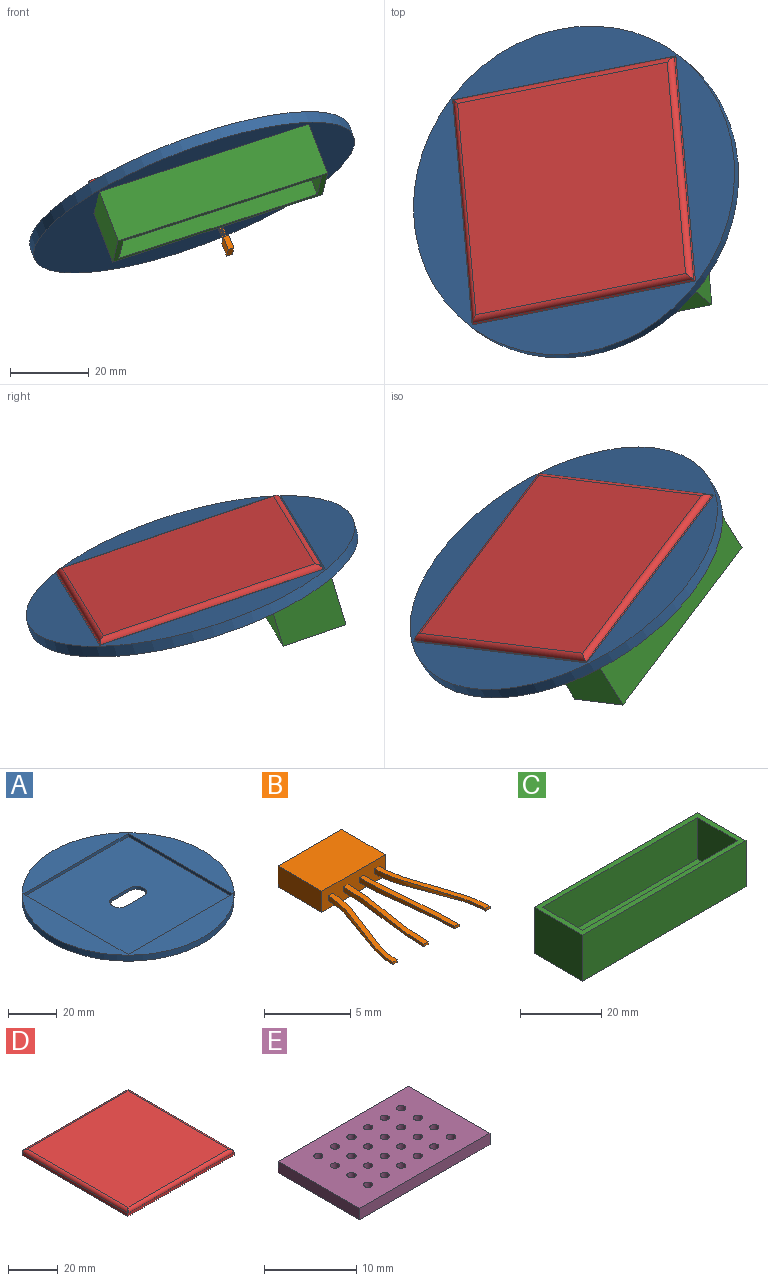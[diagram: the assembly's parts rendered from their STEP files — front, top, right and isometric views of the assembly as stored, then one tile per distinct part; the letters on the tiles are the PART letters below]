
ASSEMBLY  parts=5 mates=4
PART A: 12 faces, bbox 87x87x3 mm
  f0: plane 87x87mm, normal (0,0,1), area 2260.2mm2, adj f1,f3,f4,f5,f6
  f1: cylinder r=43.5mm len=87mm, axis (0,0,-1), area 820mm2, adj f0,f2
  f2: plane 87x87mm, normal (0,0,-1), area 5814.4mm2, adj f1,f8,f9,f10,f11
  f3: plane 60.7x1.5mm, normal (-1,0,0), area 91mm2, adj f0,f4,f6,f7
  f4: plane 60.7x1.5mm, normal (0,-1,0), area 91.1mm2, adj f0,f3,f5,f7
  f5: plane 60.7x1.5mm, normal (1,0,0), area 91mm2, adj f0,f4,f6,f7
  f6: plane 60.7x1.5mm, normal (0,1,0), area 91.1mm2, adj f0,f3,f5,f7
  f7: plane 60.7x60.7mm, normal (0,0,1), area 3554.2mm2, adj f3,f4,f5,f6,f8,f9,f10,f11
  f8: plane 10x1.5mm, normal (0,-1,0), area 15mm2, adj f2,f7,f9,f10
  f9: cylinder r=4mm len=8mm, axis (0,0,1), area 18.8mm2, adj f2,f7,f8,f11
  f10: cylinder r=4mm len=8mm, axis (0,0,1), area 18.8mm2, adj f2,f7,f8,f11
  f11: plane 10x1.5mm, normal (0,1,0), area 15mm2, adj f2,f7,f9,f10
PART B: 26 faces, bbox 8x10.8x1.5 mm
  f0: plane 3.6x1.5mm, normal (1,0,0), area 5.4mm2, adj f1,f3,f4,f5
  f1: plane 5.2x1.5mm, normal (0,1,0), area 7.8mm2, adj f0,f2,f4,f5
  f2: plane 3.6x1.5mm, normal (-1,0,0), area 5.4mm2, adj f1,f3,f4,f5
  f3: plane 5.2x1.5mm, normal (0,-1,0), area 7.3mm2, adj f0,f2,f4,f5,f7,f8,f9,f10
  f4: plane 5.2x3.6mm, normal (0,0,1), area 18.7mm2, adj f0,f1,f2,f3
  f5: plane 5.2x3.6mm, normal (0,0,-1), area 18.7mm2, adj f0,f1,f2,f3
  f6: plane 0.35x0.18mm, normal (0,-1,0), area 0.1mm2, adj f7,f8,f9,f10
  f7: bspline ~7.2x2.26mm, area 2.6mm2, adj f3,f6,f8,f10
  f8: bspline ~7.2x1.9mm, area 2mm2, adj f3,f6,f7,f9
  f9: bspline ~7.2x2.26mm, area 2.6mm2, adj f3,f6,f8,f10
  f10: bspline ~7.2x1.91mm, area 2mm2, adj f3,f6,f7,f9
  f11: plane 0.35x0.18mm, normal (0,-1,0), area 0.1mm2, adj f12,f13,f14,f15
  f12: bspline ~7.2x0.99mm, area 2.6mm2, adj f3,f11,f13,f15
  f13: bspline ~7.2x0.63mm, area 1.9mm2, adj f3,f11,f12,f14
  f14: bspline ~7.2x0.99mm, area 2.6mm2, adj f3,f11,f13,f15
  f15: bspline ~7.2x0.64mm, area 1.9mm2, adj f3,f11,f12,f14
  f16: plane 0.35x0.18mm, normal (0,-1,0), area 0.1mm2, adj f17,f18,f19,f20
  f17: bspline ~7.2x0.99mm, area 2.6mm2, adj f3,f16,f18,f20
  f18: bspline ~7.2x0.64mm, area 1.9mm2, adj f3,f16,f17,f19
  f19: bspline ~7.2x0.99mm, area 2.6mm2, adj f3,f16,f18,f20
  f20: bspline ~7.2x0.63mm, area 1.9mm2, adj f3,f16,f17,f19
  f21: plane 0.35x0.18mm, normal (0,-1,0), area 0.1mm2, adj f22,f23,f24,f25
  f22: bspline ~7.2x2.26mm, area 2.6mm2, adj f3,f21,f23,f25
  f23: bspline ~7.2x1.91mm, area 2mm2, adj f3,f21,f22,f24
  f24: bspline ~7.2x2.26mm, area 2.6mm2, adj f3,f21,f23,f25
  f25: bspline ~7.2x1.9mm, area 2mm2, adj f3,f21,f22,f24
PART C: 11 faces, bbox 57x16.9x13.9 mm
  f0: plane 57x16.9mm, normal (0,0,1), area 212.7mm2, adj f1,f2,f3,f4,f6,f7,f8,f9
  f1: plane 16.9x13.9mm, normal (1,0,0), area 234.9mm2, adj f0,f2,f4,f5
  f2: plane 57x13.9mm, normal (0,1,0), area 792.3mm2, adj f0,f1,f3,f5
  f3: plane 16.9x13.9mm, normal (-1,0,0), area 234.9mm2, adj f0,f2,f4,f5
  f4: plane 57x13.9mm, normal (0,-1,0), area 792.3mm2, adj f0,f1,f3,f5
  f5: plane 57x16.9mm, normal (0,0,-1), area 963.3mm2, adj f1,f2,f3,f4
  f6: plane 13.9x12.4mm, normal (-1,0,0), area 172.4mm2, adj f0,f7,f9,f10
  f7: plane 54x12.4mm, normal (0,-1,0), area 669.6mm2, adj f0,f6,f8,f10
  f8: plane 13.9x12.4mm, normal (1,0,0), area 172.4mm2, adj f0,f7,f9,f10
  f9: plane 54x12.4mm, normal (0,1,0), area 669.6mm2, adj f0,f6,f8,f10
  f10: plane 54x13.9mm, normal (0,0,1), area 750.6mm2, adj f6,f7,f8,f9
PART D: 20 faces, bbox 60x60x3 mm
  f0: plane 60x1.5mm, normal (1,0,0), area 90mm2, adj f1,f3,f5,f6
  f1: plane 60x1.5mm, normal (0,1,0), area 90mm2, adj f0,f2,f5,f7
  f2: plane 60x1.5mm, normal (-1,0,0), area 90mm2, adj f1,f3,f5,f9
  f3: plane 60x1.5mm, normal (0,-1,0), area 90mm2, adj f0,f2,f5,f8
  f4: plane 57x57mm, normal (0,0,1), area 3249mm2, adj f6,f7,f8,f9
  f5: plane 60x60mm, normal (0,0,-1), area 3510.9mm2, adj f0,f1,f2,f3,f10,f11,f12,f13
  f6: cylinder r=1.5mm len=60mm, axis (0,-1,0), area 138.8mm2, adj f0,f4,f7,f8
  f7: cylinder r=1.5mm len=60mm, axis (1,0,0), area 138.8mm2, adj f1,f4,f6,f9
  f8: cylinder r=1.5mm len=60mm, axis (-1,0,0), area 138.8mm2, adj f3,f4,f6,f9
  f9: cylinder r=1.5mm len=60mm, axis (0,1,0), area 138.8mm2, adj f2,f4,f7,f8
  f10: plane 8x0.5mm, normal (0,1,0), area 4mm2, adj f5,f11,f13,f14
  f11: cylinder r=2mm len=4mm, axis (0,0,-1), area 3.1mm2, adj f5,f10,f12,f14
  f12: plane 8x0.5mm, normal (0,-1,0), area 4mm2, adj f5,f11,f13,f14
  f13: cylinder r=2mm len=4mm, axis (0,0,-1), area 3.1mm2, adj f5,f10,f12,f14
  f14: plane 12x4mm, normal (0,0,-1), area 44.6mm2, adj f10,f11,f12,f13
  f15: plane 8x0.5mm, normal (0,1,0), area 4mm2, adj f5,f16,f18,f19
  f16: cylinder r=2mm len=4mm, axis (0,0,-1), area 3.1mm2, adj f5,f15,f17,f19
  f17: plane 8x0.5mm, normal (0,-1,0), area 4mm2, adj f5,f16,f18,f19
  f18: cylinder r=2mm len=4mm, axis (0,0,-1), area 3.1mm2, adj f5,f15,f17,f19
  f19: plane 12x4mm, normal (0,0,-1), area 44.6mm2, adj f15,f16,f17,f18
PART E: 30 faces, bbox 20x12.5x1.5 mm
  f0: cylinder r=0.5mm len=1.5mm, axis (0,0,1), area 4.7mm2, adj f27,f28
  f1: cylinder r=0.5mm len=1.5mm, axis (0,0,1), area 4.7mm2, adj f27,f28
  f2: cylinder r=0.5mm len=1.5mm, axis (0,0,1), area 4.7mm2, adj f27,f28
  f3: cylinder r=0.5mm len=1.5mm, axis (0,0,1), area 4.7mm2, adj f27,f28
  f4: cylinder r=0.5mm len=1.5mm, axis (0,0,1), area 4.7mm2, adj f27,f28
  f5: cylinder r=0.5mm len=1.5mm, axis (0,0,1), area 4.7mm2, adj f27,f28
  f6: cylinder r=0.5mm len=1.5mm, axis (0,0,1), area 4.7mm2, adj f27,f28
  f7: cylinder r=0.5mm len=1.5mm, axis (0,0,1), area 4.7mm2, adj f27,f28
  f8: cylinder r=0.5mm len=1.5mm, axis (0,0,1), area 4.7mm2, adj f27,f28
  f9: cylinder r=0.5mm len=1.5mm, axis (0,0,1), area 4.7mm2, adj f27,f28
  f10: cylinder r=0.5mm len=1.5mm, axis (0,0,1), area 4.7mm2, adj f27,f28
  f11: cylinder r=0.5mm len=1.5mm, axis (0,0,1), area 4.7mm2, adj f27,f28
  f12: cylinder r=0.5mm len=1.5mm, axis (0,0,1), area 4.7mm2, adj f27,f28
  f13: cylinder r=0.5mm len=1.5mm, axis (0,0,1), area 4.7mm2, adj f27,f28
  f14: cylinder r=0.5mm len=1.5mm, axis (0,0,1), area 4.7mm2, adj f27,f28
  f15: cylinder r=0.5mm len=1.5mm, axis (0,0,1), area 4.7mm2, adj f27,f28
  f16: cylinder r=0.5mm len=1.5mm, axis (0,0,1), area 4.7mm2, adj f27,f28
  f17: cylinder r=0.5mm len=1.5mm, axis (0,0,1), area 4.7mm2, adj f27,f28
  f18: cylinder r=0.5mm len=1.5mm, axis (0,0,1), area 4.7mm2, adj f27,f28
  f19: cylinder r=0.5mm len=1.5mm, axis (0,0,1), area 4.7mm2, adj f27,f28
  f20: cylinder r=0.5mm len=1.5mm, axis (0,0,1), area 4.7mm2, adj f27,f28
  f21: cylinder r=0.5mm len=1.5mm, axis (0,0,1), area 4.7mm2, adj f27,f28
  f22: cylinder r=0.5mm len=1.5mm, axis (0,0,1), area 4.7mm2, adj f27,f28
  f23: plane 12.5x1.5mm, normal (1,0,0), area 18.8mm2, adj f24,f26,f27,f28
  f24: plane 20x1.5mm, normal (0,1,0), area 30mm2, adj f23,f25,f27,f28
  f25: plane 12.5x1.5mm, normal (-1,0,0), area 18.8mm2, adj f24,f26,f27,f28
  f26: plane 20x1.5mm, normal (0,-1,0), area 30mm2, adj f23,f25,f27,f28
  f27: plane 20x12.5mm, normal (0,0,1), area 231.2mm2, adj f0,f1,f2,f3,f4,f5,f6,f7
  f28: plane 20x12.5mm, normal (0,0,-1), area 231.2mm2, adj f0,f1,f2,f3,f4,f5,f6,f7
  f29: cylinder r=0.5mm len=1.5mm, axis (0,0,1), area 4.7mm2, adj f27,f28
PLACE A rot(axis=(-0.65,-0.7,0.29),27.3deg) t=(14.86,28.8,15.64)mm
PLACE B rot(axis=(-0.6,0.34,-0.72),116.5deg) t=(22.74,41.07,3.2)mm
PLACE C rot(axis=(0.98,0.07,0.17),162.3deg) t=(16.74,7.1,23.02)mm
PLACE D rot(axis=(-0.65,-0.7,0.29),27.3deg) t=(14.24,29.29,16.92)mm
PLACE E rot(axis=(0.98,0.07,0.17),162.3deg) t=(13.64,42.95,10.83)mm
MATE fastened A.f7 <-> D.f5  axis (-0.34,0.28,0.9) through (-16.28,52.08,-1.77)mm
MATE fastened A.f2 <-> E.f28  axis (0.34,-0.28,-0.9) through (13.63,42.96,10.82)mm
MATE fastened E.f12 <-> B.f16  axis (0.34,-0.28,-0.9) through (20.37,42.48,11.88)mm
MATE fastened A.f2 <-> C.f5  axis (0.34,-0.28,-0.9) through (16.74,7.1,23.02)mm
